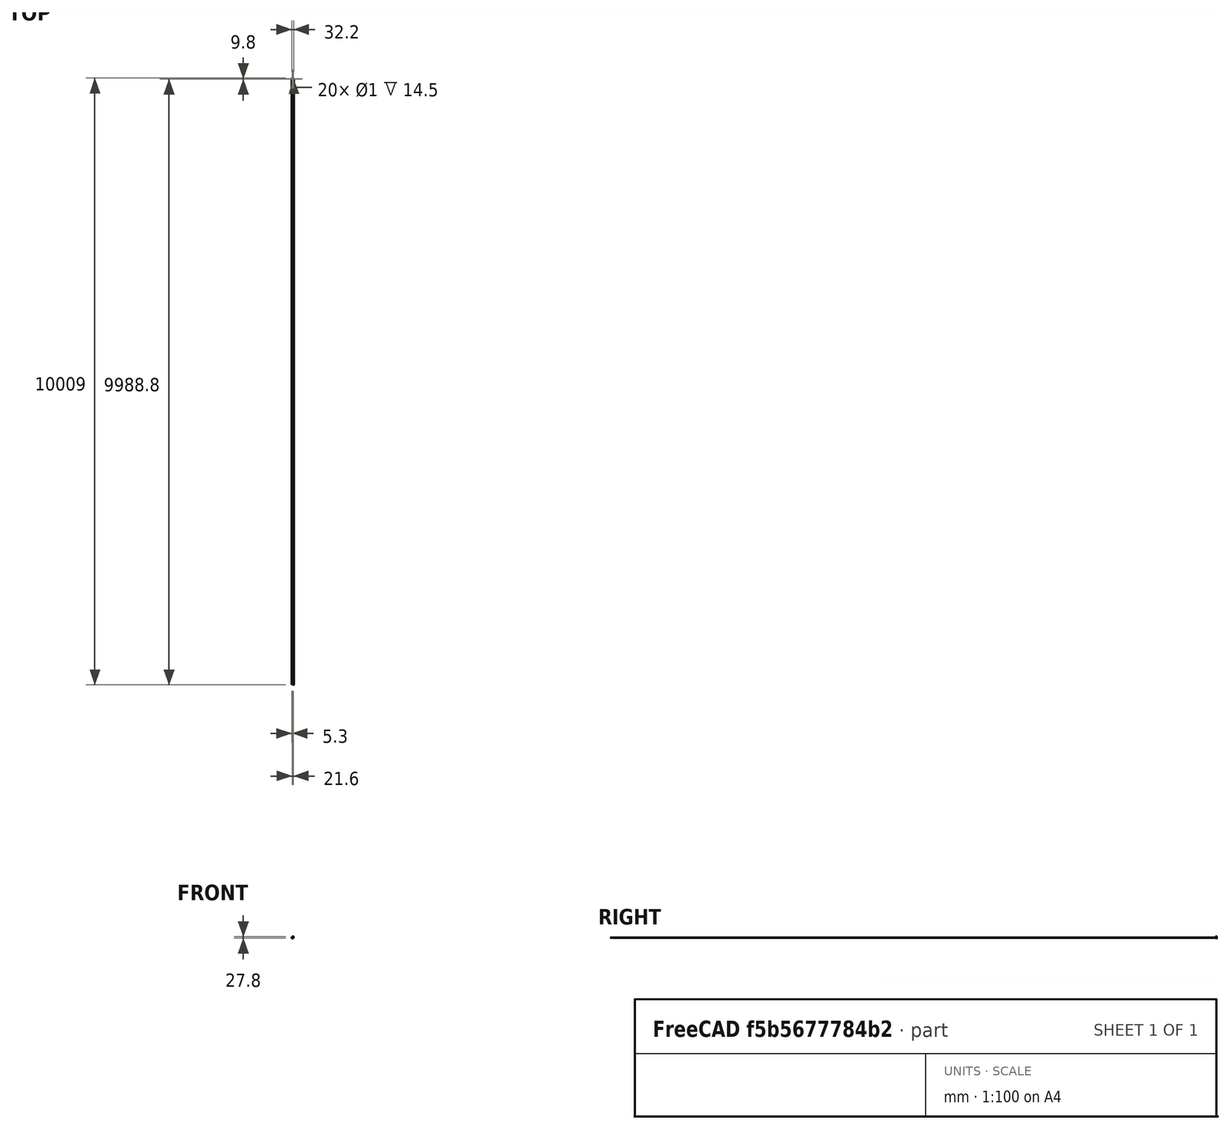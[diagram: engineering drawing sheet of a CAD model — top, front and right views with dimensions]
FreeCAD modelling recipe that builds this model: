
FCSTD DOCUMENT  (FreeCAD 0.14R3702 (Git))
Label: Emax-es08A
License: CC-BY 3.0
LicenseURL: http://creativecommons.org/licenses/by/3.0/
objects: Sketcher::SketchObject×15, PartDesign::Pocket×9, Part::Feature×6, PartDesign::Pad×4, Part::Fillet×3, App::DocumentObjectGroup×3, Part::Chamfer×2, Part::Compound×2, Part::Cylinder×1, PartDesign::PolarPattern×1, PartDesign::Revolution×1
note: 58 computed .brp shape members not serialized (recipe doc carries the construction recipe); baked Part::Feature solids carry a one-line shape summary decoded from their .brp

FEATURE [Sketcher::SketchObject] Sketch  label="main-body-sketch"
  Placement = pos=(0,0,0) rot=(1,0,0;1.5708rad)
  sketch-geometry (13):
    g0: LineSegment StartX=-11.8 StartY=-10.3 StartZ=0 EndX=-11.8 EndY=4.7 EndZ=0
    g1: LineSegment StartX=-11.8 StartY=4.7 StartZ=0 EndX=-16.1 EndY=4.7 EndZ=0
    g2: LineSegment StartX=-16.1 StartY=4.7 StartZ=0 EndX=-16.1 EndY=6.3 EndZ=0
    g3: LineSegment StartX=-16.1 StartY=6.3 StartZ=0 EndX=-11.8 EndY=6.3 EndZ=0
    g4: LineSegment StartX=-11.8 StartY=6.3 StartZ=0 EndX=-11.8 EndY=10.3 EndZ=0
    g5: LineSegment StartX=-11.8 StartY=10.3 StartZ=0 EndX=11.8 EndY=10.3 EndZ=0
    g6: LineSegment StartX=11.8 StartY=10.3 StartZ=0 EndX=11.8 EndY=6.3 EndZ=0
    g7: LineSegment StartX=11.8 StartY=6.3 StartZ=0 EndX=16.1 EndY=6.3 EndZ=0
    g8: LineSegment StartX=16.1 StartY=6.3 StartZ=0 EndX=16.1 EndY=4.7 EndZ=0
    g9: LineSegment StartX=16.1 StartY=4.7 StartZ=0 EndX=11.8 EndY=4.7 EndZ=0
    g10: LineSegment StartX=11.8 StartY=4.7 StartZ=0 EndX=11.8 EndY=-7.7 EndZ=0
    g11: LineSegment StartX=11.8 StartY=-7.7 StartZ=0 EndX=6.3 EndY=-10.3 EndZ=0
    g12: LineSegment StartX=6.3 StartY=-10.3 StartZ=0 EndX=-11.8 EndY=-10.3 EndZ=0
  constraints (37):
    c: Vertical(g0)
    c: Coincident(g0,g1)
    c: Horizontal(g1)
    c: Coincident(g1,g2)
    c: Coincident(g2,g3)
    c: Horizontal(g3)
    c: Coincident(g3,g4)
    c: Coincident(g4,g5)
    c: Horizontal(g5)
    c: Coincident(g5,g6)
    c: Vertical(g6)
    c: Coincident(g6,g7)
    c: Horizontal(g7)
    c: Coincident(g7,g8)
    c: Coincident(g8,g9)
    c: Horizontal(g9)
    c: Coincident(g9,g10)
    c: Vertical(g10)
    c: Coincident(g10,g11)
    c: Coincident(g11,g12)
    c: Horizontal(g12)
    c: Coincident(g0,g12)
    c: PointOnObject(g3,g0)
    c: Vertical(g2)
    c: Vertical(g8)
    c: Symmetric(g4,g5,g-2)
    c: Symmetric(g3,g6,g-2)
    c: Symmetric(g0,g9,g-2)
    c: DistanceX(g5) = 23.6
    c: DistanceY(g4,g0) = -20.6
    c: DistanceX(g2,g7) = 32.2
    c: DistanceY(g8) = -1.6
    c: Symmetric(g4,g0,g-1)
    c: DistanceX(g12) = -18.1
    c: DistanceY(g5,g10) = -18
    c: Symmetric(g2,g7,g-2)
    c: DistanceY(g0,g0) = -15
FEATURE [PartDesign::Pad] Pad  label="main-body"
  Length = 11.8
  Length2 = 100
  Midplane = true
  Placement = pos=(0,0,0) rot=(1,0,0;1.5708rad)
  Sketch = -> Sketch
  Type = 0
FEATURE [Sketcher::SketchObject] Sketch001  label="bottom-drills-cutout-1-sketch"
  Placement = pos=(0,0,-10.3) rot=(1,0,0;3.14159rad)
  Support = -> Pad [Face13]
  sketch-geometry (13):
    g0: Circle [constr] CenterX=-10.8 CenterY=4.9 CenterZ=0 NormalX=0 NormalY=0 NormalZ=1 Radius=0.5
    g1: LineSegment [constr] StartX=-10.8 StartY=4.9 StartZ=0 EndX=-10.8 EndY=3.9 EndZ=0
    g2: ArcOfCircle CenterX=-10.8 CenterY=4.9 CenterZ=0 NormalX=0 NormalY=0 NormalZ=1 Radius=1 StartAngle=4.71239 EndAngle=6.28319
    g3: LineSegment [constr] StartX=-10.8 StartY=4.9 StartZ=0 EndX=-9.8 EndY=4.9 EndZ=0
    g4: LineSegment StartX=-11.8 StartY=3.9 StartZ=0 EndX=-10.8 EndY=3.9 EndZ=0
    g5: LineSegment StartX=-11.8 StartY=5.9 StartZ=0 EndX=-11.8 EndY=3.9 EndZ=0
    g6: LineSegment StartX=-11.8 StartY=5.9 StartZ=0 EndX=-9.8 EndY=5.9 EndZ=0
    g7: LineSegment StartX=-9.8 StartY=5.9 StartZ=0 EndX=-9.8 EndY=4.9 EndZ=0
    g8: LineSegment StartX=-11.8 StartY=-5.9 StartZ=0 EndX=-9.8 EndY=-5.9 EndZ=0
    g9: LineSegment StartX=-10.8 StartY=-3.9 StartZ=0 EndX=-11.8 EndY=-3.9 EndZ=0
    g10: LineSegment StartX=-11.8 StartY=-3.9 StartZ=0 EndX=-11.8 EndY=-5.9 EndZ=0
    g11: LineSegment StartX=-9.8 StartY=-5.9 StartZ=0 EndX=-9.8 EndY=-4.9 EndZ=0
    g12: ArcOfCircle CenterX=-10.8 CenterY=-4.9 CenterZ=0 NormalX=0 NormalY=0 NormalZ=1 Radius=1 StartAngle=0 EndAngle=1.5708
  constraints (36):
    c: Radius(g0) = 0.5
    c: Vertical(g1)
    c: DistanceY(g1) = -1
    c: Coincident(g0,g1)
    c: DistanceY(g-1,g0) = 4.9
    c: Coincident(g2,g0)
    c: Coincident(g2,g1)
    c: Coincident(g3,g0)
    c: Horizontal(g3)
    c: Coincident(g3,g2)
    c: Horizontal(g4)
    c: Coincident(g4,g1)
    c: Vertical(g5)
    c: Coincident(g4,g5)
    c: DistanceX(g-1,g5) = -11.8
    c: DistanceY(g-1,g5) = 5.9
    c: Coincident(g6,g5)
    c: Horizontal(g6)
    c: Vertical(g7)
    c: Coincident(g7,g6)
    c: Coincident(g7,g2)
    c: DistanceX(g0,g5) = -1
    c: Coincident(g9,g10)
    c: Coincident(g10,g8)
    c: Horizontal(g8)
    c: Horizontal(g9)
    c: Vertical(g10)
    c: Coincident(g11,g8)
    c: Coincident(g9,g12)
    c: Coincident(g12,g11)
    c: Vertical(g11)
    c: Symmetric(g9,g4,g-1)
    c: Symmetric(g8,g5,g-1)
    c: Symmetric(g1,g9,g-1)
    c: Symmetric(g12,g0,g-1)
    c: Symmetric(g11,g2,g-1)
FEATURE [Sketcher::SketchObject] Sketch004
  Placement = pos=(0,0,2.7) rot=(0,0,1;3.14159rad)
  sketch-geometry (1):
    g0: Circle CenterX=-10.75 CenterY=4.85 CenterZ=0 NormalX=0 NormalY=0 NormalZ=1 Radius=0.5
  constraints (1):
    c: Radius(g0) = 0.5
FEATURE [PartDesign::Pocket] Pocket  label="bottom-drills-cutout-1"
  Length = 0.6
  Placement = pos=(0,0,0) rot=(1,0,0;1.5708rad)
  Sketch = -> Sketch001
  Type = 0
FEATURE [Sketcher::SketchObject] Sketch005  label="bottom-drills-cutout-2"
  ExternalGeometry = -> [Pocket]
  Placement = pos=(0,0,-10.3) rot=(1,0,0;3.14159rad)
  Support = -> Pocket [Face9]
  sketch-geometry (12):
    g0: LineSegment StartX=9.8 StartY=5.9 StartZ=0 EndX=11.8 EndY=5.9 EndZ=0
    g1: LineSegment StartX=11.8 StartY=5.9 StartZ=0 EndX=11.8 EndY=3.9 EndZ=0
    g2: LineSegment StartX=9.8 StartY=4.9 StartZ=0 EndX=9.8 EndY=5.9 EndZ=0
    g3: LineSegment StartX=10.8 StartY=3.9 StartZ=0 EndX=11.8 EndY=3.9 EndZ=0
    g4: ArcOfCircle CenterX=10.8 CenterY=4.9 CenterZ=0 NormalX=0 NormalY=0 NormalZ=1 Radius=1 StartAngle=3.14159 EndAngle=4.71239
    g5: LineSegment [constr] StartX=10.8 StartY=4.9 StartZ=0 EndX=10.8 EndY=3.9 EndZ=0
    g6: LineSegment [constr] StartX=9.8 StartY=4.9 StartZ=0 EndX=10.8 EndY=4.9 EndZ=0
    g7: LineSegment StartX=9.8 StartY=-5.9 StartZ=0 EndX=11.8 EndY=-5.9 EndZ=0
    g8: LineSegment StartX=11.8 StartY=-5.9 StartZ=0 EndX=11.8 EndY=-3.9 EndZ=0
    g9: LineSegment StartX=11.8 StartY=-3.9 StartZ=0 EndX=10.8 EndY=-3.9 EndZ=0
    g10: LineSegment StartX=9.8 StartY=-5.9 StartZ=0 EndX=9.8 EndY=-4.9 EndZ=0
    g11: ArcOfCircle CenterX=10.8 CenterY=-4.9 CenterZ=0 NormalX=0 NormalY=0 NormalZ=1 Radius=1 StartAngle=1.5708 EndAngle=3.14159
  constraints (33):
    c: Coincident(g0,g1)
    c: Coincident(g2,g0)
    c: Horizontal(g0)
    c: Vertical(g1)
    c: Vertical(g2)
    c: Coincident(g-3,g0)
    c: Horizontal(g3)
    c: Coincident(g3,g1)
    c: DistanceX(g4,g0) = 1
    c: DistanceY(g0,g4) = -1
    c: Coincident(g4,g2)
    c: Coincident(g4,g3)
    c: Vertical(g5)
    c: Coincident(g5,g3)
    c: Coincident(g4,g5)
    c: Horizontal(g6)
    c: Coincident(g6,g4)
    c: Coincident(g6,g2)
    c: Radius(g4) = 1
    c: Coincident(g7,g8)
    c: Coincident(g8,g9)
    c: Horizontal(g9)
    c: Horizontal(g7)
    c: Vertical(g8)
    c: Symmetric(g8,g1,g-1)
    c: Symmetric(g7,g0,g-1)
    c: Symmetric(g7,g0,g-1)
    c: Coincident(g7,g10)
    c: Vertical(g10)
    c: Coincident(g9,g11)
    c: Coincident(g11,g10)
    c: Symmetric(g11,g4,g-1)
    c: Symmetric(g10,g2,g-1)
FEATURE [PartDesign::Pocket] Pocket001  label="bottom-drills-cutout-003"
  Length = 3.2
  Placement = pos=(0,0,0) rot=(1,0,0;1.5708rad)
  Sketch = -> Sketch005
  Type = 0
FEATURE [Sketcher::SketchObject] Sketch006  label="bottom-drills-1-sketch"
  Placement = pos=(0,0,-9.7) rot=(1,0,0;3.14159rad)
  Support = -> Pocket001 [Face7]
  sketch-geometry (2):
    g0: Circle CenterX=-10.8 CenterY=4.9 CenterZ=0 NormalX=0 NormalY=0 NormalZ=1 Radius=0.5
    g1: Circle CenterX=-10.8 CenterY=-4.9 CenterZ=0 NormalX=0 NormalY=0 NormalZ=1 Radius=0.5
  constraints (5):
    c: Radius(g0) = 0.5
    c: DistanceX(g-1,g0) = -10.8
    c: DistanceY(g-1,g0) = 4.9
    c: Equal(g1,g0)
    c: Symmetric(g1,g0,g-1)
FEATURE [PartDesign::Pocket] Pocket002  label="bottom-drills-1"
  Length = 14.5
  Placement = pos=(0,0,0) rot=(1,0,0;1.5708rad)
  Sketch = -> Sketch006
  Type = 0
FEATURE [Sketcher::SketchObject] Sketch007  label="bottom-drills-2-sketch"
  Placement = pos=(0,0,-7.1) rot=(1,0,0;3.14159rad)
  Support = -> Pocket002 [Face27]
  sketch-geometry (2):
    g0: Circle CenterX=10.8 CenterY=4.9 CenterZ=0 NormalX=0 NormalY=0 NormalZ=1 Radius=0.5
    g1: Circle CenterX=10.8 CenterY=-4.9 CenterZ=0 NormalX=0 NormalY=0 NormalZ=1 Radius=0.5
  constraints (5):
    c: Radius(g0) = 0.5
    c: DistanceX(g-1,g0) = 10.8
    c: DistanceY(g-1,g0) = 4.9
    c: Equal(g1,g0)
    c: Symmetric(g1,g0,g-1)
FEATURE [PartDesign::Pocket] Pocket003  label="bottom-drills-2"
  Length = 14.5
  Placement = pos=(0,0,0) rot=(1,0,0;1.5708rad)
  Sketch = -> Sketch007
  Type = 0
FEATURE [Sketcher::SketchObject] Sketch003  label="servo-ears-drill-sketch"
  Placement = pos=(0,0,6.3) rot=(0,0,1;3.14159rad)
  Support = -> Pocket003 [Face23]
  sketch-geometry (2):
    g0: Circle CenterX=-13.8 CenterY=0 CenterZ=0 NormalX=0 NormalY=0 NormalZ=1 Radius=1
    g1: Circle CenterX=13.8 CenterY=0 CenterZ=0 NormalX=0 NormalY=0 NormalZ=1 Radius=1
  constraints (5):
    c: Radius(g0) = 1
    c: Equal(g0,g1)
    c: Symmetric(g0,g1,g-2)
    c: PointOnObject(g0,g-1)
    c: DistanceX(g-1,g0) = -13.8
FEATURE [PartDesign::Pocket] Pocket004  label="servo-ears-drill"
  Length = 5
  Placement = pos=(0,0,0) rot=(1,0,0;1.5708rad)
  Sketch = -> Sketch003
  Type = 1
FEATURE [Sketcher::SketchObject] Sketch008  label="top-base-1-sketch"
  ExternalGeometry = -> [Pocket004]
  Placement = pos=(0,0,10.3) rot=(0,0,1;3.14159rad)
  Support = -> Pocket004 [Face21]
  sketch-geometry (10):
    g0: LineSegment [constr] StartX=-11.45 StartY=5.9 StartZ=0 EndX=-11.45 EndY=0 EndZ=0
    g1: Circle [constr] CenterX=0 CenterY=0 CenterZ=0 NormalX=0 NormalY=0 NormalZ=1 Radius=3.2
    g2: Circle [constr] CenterX=-5.85 CenterY=0 CenterZ=0 NormalX=0 NormalY=0 NormalZ=1 Radius=5.6
    g3: ArcOfCircle CenterX=-0.5 CenterY=4.76302 CenterZ=0 NormalX=0 NormalY=0 NormalZ=1 Radius=1.56302 StartAngle=3.86901 EndAngle=4.71239
    g4: LineSegment [constr] StartX=-0.5 StartY=5.9 StartZ=0 EndX=-0.5 EndY=0 EndZ=0
    g5: LineSegment StartX=-0.5 StartY=3.2 StartZ=0 EndX=0 EndY=3.2 EndZ=0
    g6: LineSegment StartX=-0.5 StartY=-3.2 StartZ=0 EndX=0 EndY=-3.2 EndZ=0
    g7: ArcOfCircle CenterX=-0.5 CenterY=-4.76302 CenterZ=0 NormalX=0 NormalY=0 NormalZ=1 Radius=1.56302 StartAngle=1.5708 EndAngle=2.41417
    g8: ArcOfCircle CenterX=0 CenterY=0 CenterZ=0 NormalX=0 NormalY=0 NormalZ=1 Radius=3.2 StartAngle=4.71239 EndAngle=7.85398
    g9: ArcOfCircle CenterX=-5.85 CenterY=0 CenterZ=0 NormalX=0 NormalY=0 NormalZ=1 Radius=5.6 StartAngle=0.727421 EndAngle=5.55576
  constraints (32):
    c: Vertical(g0)
    c: PointOnObject(g0,g-3)
    c: PointOnObject(g0,g-1)
    c: DistanceX(g-3,g0) = 0.35
    c: Coincident(g1,g-1)
    c: Radius(g1) = 3.2
    c: PointOnObject(g2,g-1)
    c: Radius(g2) = 5.6
    c: PointOnObject(g0,g2)
    c: Vertical(g4)
    c: PointOnObject(g4,g-1)
    c: PointOnObject(g4,g-3)
    c: DistanceX(g-1,g4) = -0.5
    c: Horizontal(g5)
    c: PointOnObject(g5,g-2)
    c: PointOnObject(g5,g4)
    c: Tangent(g5,g1)
    c: Coincident(g3,g5)
    c: PointOnObject(g3,g4)
    c: Tangent(g3,g2)
    c: Horizontal(g6)
    c: Symmetric(g5,g6,g-1)
    c: Symmetric(g6,g3,g-1)
    c: Symmetric(g7,g3,g-1)
    c: Coincident(g7,g6)
    c: Symmetric(g7,g3,g-1)
    c: Coincident(g8,g-1)
    c: Coincident(g8,g5)
    c: Coincident(g8,g6)
    c: Coincident(g9,g2)
    c: Coincident(g9,g3)
    c: Coincident(g9,g7)
FEATURE [PartDesign::Pad] Pad001  label="top-base-1"
  Length = 3.4
  Length2 = 100
  Placement = pos=(0,0,0) rot=(1,0,0;1.5708rad)
  Sketch = -> Sketch008
  Type = 0
FEATURE [Sketcher::SketchObject] Sketch009  label="top-detail-1-sketch"
  Placement = pos=(0,0,13.7) rot=(0,0,1;3.14159rad)
  Support = -> Pad001 [Face47]
  sketch-geometry (1):
    g0: Circle CenterX=0 CenterY=0 CenterZ=0 NormalX=0 NormalY=0 NormalZ=1 Radius=1
  constraints (3):
    c: PointOnObject(g0,g-1)
    c: Radius(g0) = 1
    c: Coincident(g0,g-1)
FEATURE [PartDesign::Pad] Pad002  label="top-detail-1"
  Length = 1.4
  Length2 = 100
  Placement = pos=(0,0,0) rot=(1,0,0;1.5708rad)
  Sketch = -> Sketch009
  Type = 0
FEATURE [Sketcher::SketchObject] Sketch010  label="top-detail-2-sketch"
  Placement = pos=(0,0,13.7) rot=(0,0,1;3.14159rad)
  Support = -> Pad002 [Face47]
  sketch-geometry (1):
    g0: Circle CenterX=-5.85 CenterY=0 CenterZ=0 NormalX=0 NormalY=0 NormalZ=1 Radius=2.65
  constraints (3):
    c: PointOnObject(g0,g-1)
    c: DistanceX(g-1,g0) = -5.85
    c: Radius(g0) = 2.65
FEATURE [PartDesign::Pad] Pad003  label="top-detail-2"
  Length = 0.3
  Length2 = 100
  Placement = pos=(0,0,0) rot=(1,0,0;1.5708rad)
  Sketch = -> Sketch010
  Type = 0
FEATURE [Sketcher::SketchObject] Sketch011  label="shaft-cutout-sketch"
  Placement = pos=(0,0,14) rot=(0,0,1;3.14159rad)
  Support = -> Pad003 [Face52]
  sketch-geometry (1):
    g0: Circle CenterX=-5.85 CenterY=0 CenterZ=0 NormalX=0 NormalY=0 NormalZ=1 Radius=1.9
  constraints (3):
    c: PointOnObject(g0,g-1)
    c: Radius(g0) = 1.9
    c: DistanceX(g-1,g0) = -5.85
FEATURE [PartDesign::Pocket] Pocket005  label="shaft-cutout"
  Length = 5
  Placement = pos=(0,0,0) rot=(1,0,0;1.5708rad)
  Sketch = -> Sketch011
  Type = 0
FEATURE [Part::Chamfer] Chamfer
  Base = -> Pocket005
  Edges = 1 edges r=0.295: [Edge125]
FEATURE [Part::Fillet] Fillet
  Base = -> Chamfer
  Edges = 6 edges r=0.2: [Edge2,Edge3,Edge4,Edge5,Edge6,Edge7]
FEATURE [Part::Fillet] Fillet001
  Base = -> Fillet
  Edges = 19 edges r=0.3: [Edge39,Edge40,Edge41,Edge42,Edge45,Edge46,Edge49,Edge50,Edge53,Edge57,Edge61,Edge64,Edge65,Edge68,Edge72,Edge76,Edge91,Edge95,Edge102]
FEATURE [Part::Fillet] Fillet002
  Base = -> Fillet001
  Edges = 4 edges r=1: [Edge49,Edge59,Edge71,Edge81]
FEATURE [Sketcher::SketchObject] Sketch012  label="top-plate-sketch"
  Placement = pos=(0,0,10.3) rot=(0,0,1;0rad)
  Support = -> Fillet002 [Face32]
  sketch-geometry (4):
    g0: LineSegment StartX=-10.5 StartY=4.6 StartZ=0 EndX=-4.7 EndY=4.6 EndZ=0
    g1: LineSegment StartX=-4.7 StartY=4.6 StartZ=0 EndX=-4.7 EndY=-4.6 EndZ=0
    g2: LineSegment StartX=-4.7 StartY=-4.6 StartZ=0 EndX=-10.5 EndY=-4.6 EndZ=0
    g3: LineSegment StartX=-10.5 StartY=-4.6 StartZ=0 EndX=-10.5 EndY=4.6 EndZ=0
  constraints (12):
    c: Coincident(g0,g1)
    c: Coincident(g1,g2)
    c: Coincident(g2,g3)
    c: Coincident(g3,g0)
    c: Horizontal(g0)
    c: Horizontal(g2)
    c: Vertical(g1)
    c: Vertical(g3)
    c: Symmetric(g0,g1,g-1)
    c: DistanceY(g1) = -9.2
    c: DistanceX(g0) = 5.8
    c: DistanceX(g-1,g0) = -4.7
FEATURE [PartDesign::Pocket] Pocket006  label="top-plate"
  Length = 0.1
  Sketch = -> Sketch012
  Type = 0
FEATURE [App::DocumentObjectGroup] Group  label="main-servo-src"
  Group = -> [Pad,Sketch004,Pocket,Pocket001,Pocket002,Pocket003,Pocket004,Pad001,Pad002,Pad003,Fillet002,Pocket006]
FEATURE [Part::Feature] Pocket006001  label="main-servo"
  shape: bbox 32.2 x 12.1 x 25.4 mm, 95 faces (baked)
FEATURE [Part::Cylinder] Cylinder
  Angle = 360
  Height = 8.4
  Radius = 1.9
FEATURE [Part::Chamfer] Chamfer001
  Base = -> Cylinder
  Edges = 1 edges r=0.1: [Edge1]
FEATURE [Sketcher::SketchObject] Sketch013  label="slot-sketch"
  Placement = pos=(0,0,8.4) rot=(0,0,1;0rad)
  Support = -> Chamfer001 [Face4]
  sketch-geometry (1):
    g0: Circle CenterX=0 CenterY=2.1 CenterZ=0 NormalX=0 NormalY=0 NormalZ=1 Radius=0.35
  constraints (3):
    c: Radius(g0) = 0.35
    c: DistanceY(g-1,g0) = 2.1
    c: PointOnObject(g0,g-2)
FEATURE [PartDesign::Pocket] Pocket006002  label="slot-master"
  Length = 5
  Sketch = -> Sketch013
  Type = 1
FEATURE [PartDesign::PolarPattern] PolarPattern  label="slots"
  Angle = 360
  Axis = -> Sketch013 [N_Axis]
  Occurrences = 16
  Originals = -> [Pocket006002]
FEATURE [App::DocumentObjectGroup] Group001  label="servo-shaft-src"
  Group = -> [Chamfer001,Pocket006002,PolarPattern]
FEATURE [Part::Feature] PolarPattern001  label="servo-shaft"
  Placement = pos=(5.85,0,9) rot=(0,0,1;0rad)
  shape: bbox 3.784 x 3.784 x 8.4 mm, 50 faces (baked)
FEATURE [Sketcher::SketchObject] Sketch014  label="screw-body-sketch"
  Placement = pos=(0,0,0) rot=(-1,0,0;4.71239rad)
  sketch-geometry (6):
    g0: LineSegment StartX=0 StartY=15.3 StartZ=0 EndX=0.9 EndY=15.3 EndZ=0
    g1: LineSegment StartX=0.9 StartY=15.3 StartZ=0 EndX=0.9 EndY=14.6 EndZ=0
    g2: LineSegment StartX=0.9 StartY=14.6 StartZ=0 EndX=0.46 EndY=14.6 EndZ=0
    g3: LineSegment StartX=0.46 StartY=14.6 StartZ=0 EndX=0.46 EndY=1.2 EndZ=0
    g4: LineSegment StartX=0.46 StartY=1.2 StartZ=0 EndX=0 EndY=0 EndZ=0
    g5: LineSegment StartX=0 StartY=0 StartZ=0 EndX=0 EndY=15.3 EndZ=0
  constraints (17):
    c: Coincident(g0,g1)
    c: Coincident(g1,g2)
    c: Coincident(g2,g3)
    c: Coincident(g3,g4)
    c: Coincident(g4,g5)
    c: Coincident(g5,g0)
    c: Horizontal(g0)
    c: Vertical(g1)
    c: Horizontal(g2)
    c: Vertical(g3)
    c: Vertical(g5)
    c: Coincident(g4,g-1)
    c: DistanceX(g-1,g2) = 0.46
    c: DistanceY(g1) = -0.7
    c: DistanceX(g0) = 0.9
    c: DistanceY(g5) = 15.3
    c: DistanceY(g-1,g3) = 1.2
FEATURE [PartDesign::Revolution] Revolution  label="screw-body"
  Angle = 360
  Axis = (0,0,1)
  Base = (0,0,0)
  Placement = pos=(0,0,0) rot=(-1,0,0;4.71239rad)
  ReferenceAxis = -> Sketch014 [V_Axis]
  Reversed = true
  Sketch = -> Sketch014
FEATURE [Sketcher::SketchObject] Sketch015  label="top-cross-sketch"
  Placement = pos=(0,0,15.3) rot=(0,0,1;3.14159rad)
  Support = -> Revolution [Face1]
  sketch-geometry (12):
    g0: LineSegment StartX=-0.7 StartY=-0.2 StartZ=0 EndX=-0.7 EndY=0.2 EndZ=0
    g1: LineSegment StartX=-0.7 StartY=0.2 StartZ=0 EndX=-0.2 EndY=0.2 EndZ=0
    g2: LineSegment StartX=-0.2 StartY=0.2 StartZ=0 EndX=-0.2 EndY=0.7 EndZ=0
    g3: LineSegment StartX=-0.2 StartY=0.7 StartZ=0 EndX=0.2 EndY=0.7 EndZ=0
    g4: LineSegment StartX=0.2 StartY=0.7 StartZ=0 EndX=0.2 EndY=0.2 EndZ=0
    g5: LineSegment StartX=0.2 StartY=0.2 StartZ=0 EndX=0.7 EndY=0.2 EndZ=0
    g6: LineSegment StartX=0.7 StartY=0.2 StartZ=0 EndX=0.7 EndY=-0.2 EndZ=0
    g7: LineSegment StartX=0.7 StartY=-0.2 StartZ=0 EndX=0.2 EndY=-0.2 EndZ=0
    g8: LineSegment StartX=0.2 StartY=-0.2 StartZ=0 EndX=0.2 EndY=-0.7 EndZ=0
    g9: LineSegment StartX=0.2 StartY=-0.7 StartZ=0 EndX=-0.2 EndY=-0.7 EndZ=0
    g10: LineSegment StartX=-0.2 StartY=-0.7 StartZ=0 EndX=-0.2 EndY=-0.2 EndZ=0
    g11: LineSegment StartX=-0.2 StartY=-0.2 StartZ=0 EndX=-0.7 EndY=-0.2 EndZ=0
  constraints (33):
    c: Coincident(g0,g1)
    c: Coincident(g1,g2)
    c: Coincident(g2,g3)
    c: Equal(g1,g2)
    c: Horizontal(g1)
    c: Horizontal(g3)
    c: Vertical(g0)
    c: Equal(g0,g3)
    c: Vertical(g2)
    c: Coincident(g4,g5)
    c: Coincident(g5,g6)
    c: Coincident(g6,g7)
    c: Coincident(g7,g8)
    c: Coincident(g8,g9)
    c: Coincident(g9,g10)
    c: Coincident(g10,g11)
    c: Vertical(g10)
    c: Vertical(g8)
    c: Vertical(g4)
    c: Vertical(g6)
    c: Horizontal(g7)
    c: Horizontal(g9)
    c: Horizontal(g11)
    c: Horizontal(g5)
    c: Coincident(g11,g0)
    c: Coincident(g4,g3)
    c: Symmetric(g1,g7,g-1)
    c: Symmetric(g1,g4,g-2)
    c: Symmetric(g10,g7,g-2)
    c: Symmetric(g0,g5,g-2)
    c: Symmetric(g3,g8,g-1)
    c: DistanceX(g0,g5) = 1.4
    c: DistanceX(g3) = 0.4
FEATURE [PartDesign::Pocket] Pocket006003  label="top-cross"
  Length = 0.5
  Placement = pos=(0,0,0) rot=(-1,0,0;4.71239rad)
  Sketch = -> Sketch015
  Type = 0
FEATURE [App::DocumentObjectGroup] Group002  label="servo-bottom-screw-src"
  Group = -> [Revolution,Pocket006003]
FEATURE [Part::Feature] Pocket006003001  label="bottom-screw-1"
  Placement = pos=(10.8,4.9,7.5) rot=(-1,0,0;1.5708rad)
  shape: bbox 1.8 x 1.8 x 15.3 mm, 18 faces (baked)
FEATURE [Part::Feature] Pocket006003002  label="bottom-screw-002"
  Placement = pos=(-10.8,-4.9,4.9) rot=(-1,0,0;1.5708rad)
  shape: bbox 1.8 x 1.8 x 15.3 mm, 18 faces (baked)
FEATURE [Part::Feature] Pocket006003003  label="bottom-screw-003"
  Placement = pos=(-10.8,4.9,4.9) rot=(-1,0,0;1.5708rad)
  shape: bbox 1.8 x 1.8 x 15.3 mm, 18 faces (baked)
FEATURE [Part::Feature] Pocket006003004  label="bottom-screw-004"
  Placement = pos=(10.8,-4.9,7.5) rot=(-1,0,0;1.5708rad)
  shape: bbox 1.8 x 1.8 x 15.3 mm, 18 faces (baked)
FEATURE [Part::Compound] Compound  label="Emax-es08A"
  Links = -> [Pocket006001,PolarPattern001,Pocket006003001,Pocket006003002,Pocket006003003,Pocket006003004]
FEATURE [Part::Compound] Compound001  label="Emax-es08A-final"
